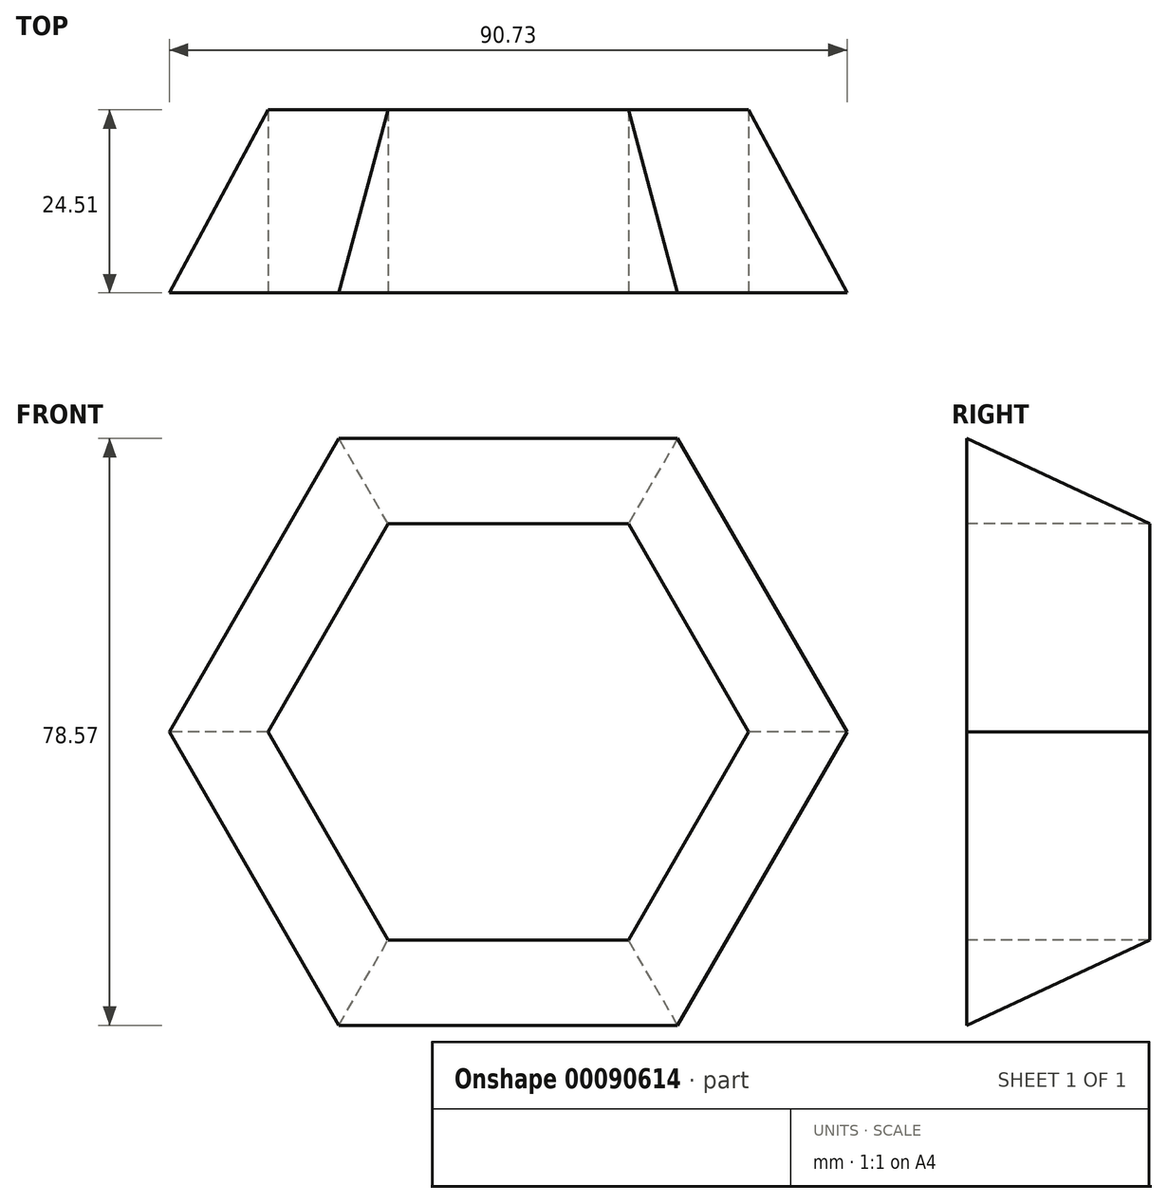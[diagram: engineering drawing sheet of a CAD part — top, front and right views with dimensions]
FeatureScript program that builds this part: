
annotation { "Feature Type Name" : "Feature", "Feature Type Description" : "" }
export const myFeature = defineFeature(function(context is Context, id is Id, definition is map)
    precondition{}
    {
        {
            var Q0;
            Q0=qCreatedBy(makeId("Front.planeOp"),FACE);
            var sketch = newSketch(context, id + "F0", { "sketchPlane" : qUnion([Q0])});
            skCircle(sketch, "E0.cCircle", {"center": v(-15.61, 18.56) * mm, "radius": 39.28 * mm, "construction": true});
            skLineSegment(sketch, "E0.0", {"start": v(-38.3, 57.84) * mm, "end": v(7.07, 57.84) * mm});
            skLineSegment(sketch, "E0.1", {"start": v(7.07, 57.84) * mm, "end": v(29.75, 18.56) * mm});
            skLineSegment(sketch, "E0.2", {"start": v(29.75, 18.56) * mm, "end": v(7.07, -20.73) * mm});
            skLineSegment(sketch, "E0.3", {"start": v(7.07, -20.73) * mm, "end": v(-38.3, -20.73) * mm});
            skLineSegment(sketch, "E0.4", {"start": v(-38.3, -20.73) * mm, "end": v(-60.98, 18.56) * mm});
            skLineSegment(sketch, "E0.5", {"start": v(-60.98, 18.56) * mm, "end": v(-38.3, 57.84) * mm});
            skPoint(sketch, "E0.0.midPoint", {"position": v(-15.61, 57.84) * mm});
            skCircle(sketch, "E1.cCircle", {"center": v(-15.61, 18.56) * mm, "radius": 27.85 * mm, "construction": true});
            skLineSegment(sketch, "E1.0", {"start": v(0.47, -9.3) * mm, "end": v(-31.7, -9.3) * mm});
            skLineSegment(sketch, "E1.1", {"start": v(-31.7, -9.3) * mm, "end": v(-47.78, 18.56) * mm});
            skLineSegment(sketch, "E1.2", {"start": v(-47.78, 18.56) * mm, "end": v(-31.7, 46.4) * mm});
            skLineSegment(sketch, "E1.3", {"start": v(-31.7, 46.4) * mm, "end": v(0.47, 46.4) * mm});
            skLineSegment(sketch, "E1.4", {"start": v(0.47, 46.4) * mm, "end": v(16.55, 18.56) * mm});
            skLineSegment(sketch, "E1.5", {"start": v(16.55, 18.56) * mm, "end": v(0.47, -9.3) * mm});
            skPoint(sketch, "E1.0.midPoint", {"position": v(-15.61, -9.3) * mm});
            skSolve(sketch);
        }
        {
            var Q0;
            Q0=makeQuery(id+"F0.imprint","IMPRINT",FACE,{"disambiguationData":[TD([[makeQuery(id+"F0.imprint","IMPRINT",EDGE,{"derivedFrom":sQuery(id+"F0.wireOp",EDGE,"E0.0")}),-1.0]])]});
            extrude(context, id + "F1", {"entities" : qUnion([Q0]), "oppositeDirection" : true, "depth" : 25.4 * mm});
        }
        {
            var Q0;
            Q0=makeQuery(id+"F1.opExtrude","CAP_EDGE",EDGE,{"disambiguationData":[OSD([sQuery(id+"F0.wireOp",EDGE,"E0.0")])],"isStart":false});
            var Q1;
            Q1=makeQuery(id+"F1.opExtrude","CAP_EDGE",EDGE,{"disambiguationData":[OSD([sQuery(id+"F0.wireOp",EDGE,"E0.5")])],"isStart":false});
            var Q2;
            Q2=makeQuery(id+"F1.opExtrude","CAP_EDGE",EDGE,{"disambiguationData":[OSD([sQuery(id+"F0.wireOp",EDGE,"E0.1")])],"isStart":false});
            var Q3;
            Q3=makeQuery(id+"F1.opExtrude","CAP_EDGE",EDGE,{"disambiguationData":[OSD([sQuery(id+"F0.wireOp",EDGE,"E0.2")])],"isStart":false});
            var Q4;
            Q4=makeQuery(id+"F1.opExtrude","CAP_EDGE",EDGE,{"disambiguationData":[OSD([sQuery(id+"F0.wireOp",EDGE,"E0.3")])],"isStart":false});
            var Q5;
            Q5=makeQuery(id+"F1.opExtrude","CAP_EDGE",EDGE,{"disambiguationData":[OSD([sQuery(id+"F0.wireOp",EDGE,"E0.4")])],"isStart":false});
            chamfer(context, id + "F2", {"entities" : qUnion([Q0, Q1, Q2, Q3, Q4, Q5]), "chamferType" : ChamferType.OFFSET_ANGLE, "width" : 25.4 * mm, "oppositeDirection" : true, "angle" : 25 * degree, "tangentPropagation" : true});
        }
    });
